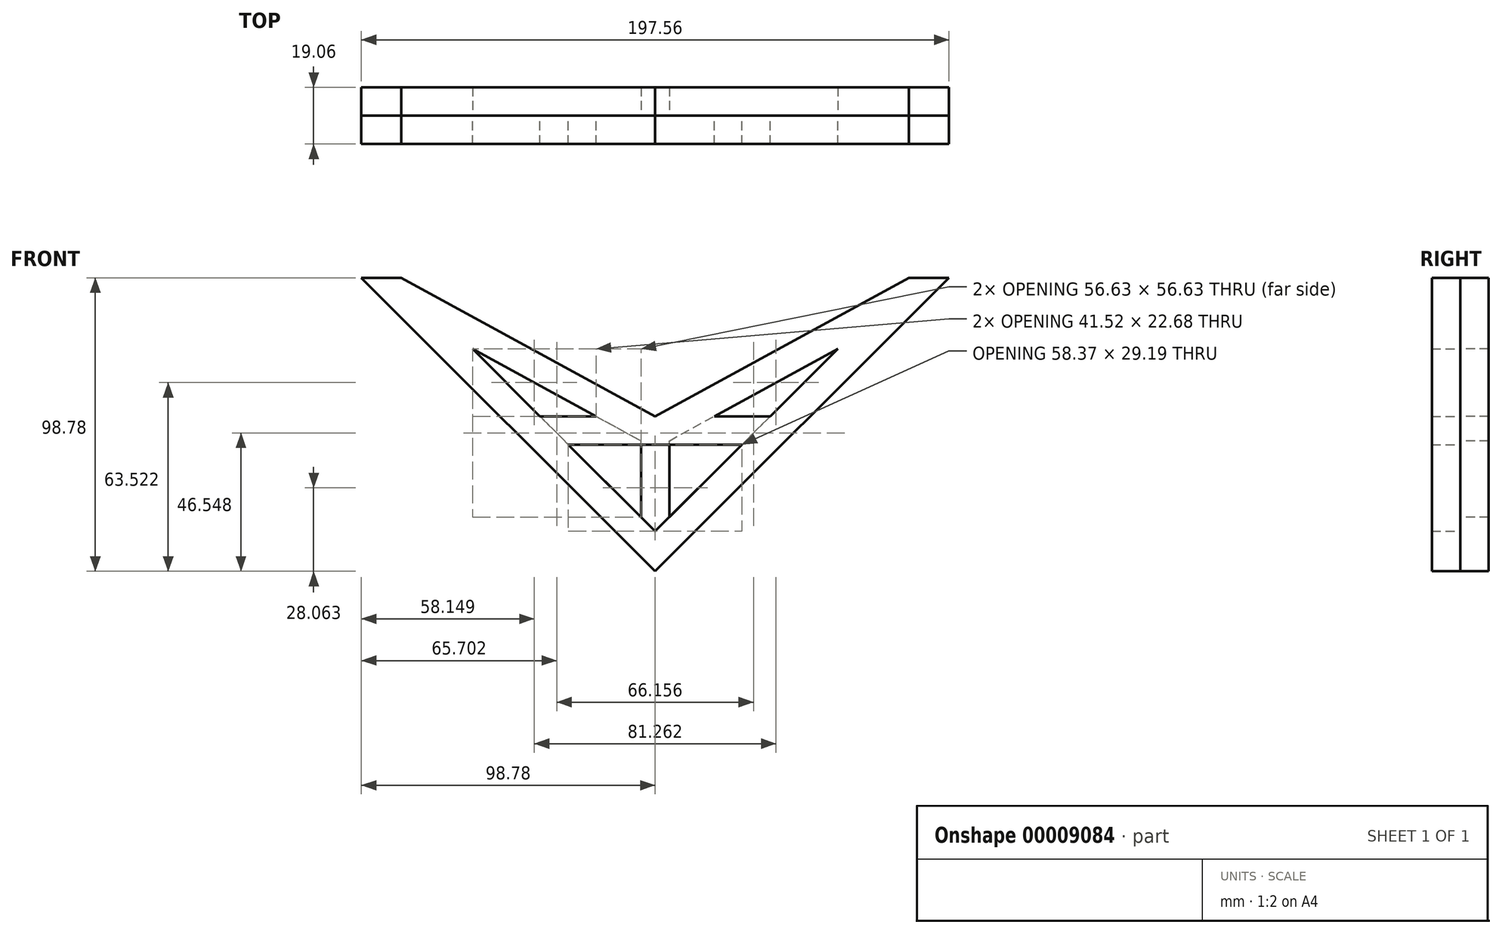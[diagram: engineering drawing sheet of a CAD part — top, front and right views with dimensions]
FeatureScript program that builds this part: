
annotation { "Feature Type Name" : "Feature", "Feature Type Description" : "" }
export const myFeature = defineFeature(function(context is Context, id is Id, definition is map)
    precondition{}
    {
        {
            var Q0;
            Q0=qCreatedBy(makeId("Front.planeOp"),FACE);
            var sketch = newSketch(context, id + "F0", { "sketchPlane" : qUnion([Q0])});
            skLineSegment(sketch, "E0", {"start": v(0, 0) * mm, "end": v(-98.78, 98.78) * mm});
            skLineSegment(sketch, "E1", {"start": v(0, 0) * mm, "end": v(98.78, 98.78) * mm});
            skLineSegment(sketch, "E2", {"start": v(0, 13.47) * mm, "end": v(-29.19, 42.66) * mm});
            skLineSegment(sketch, "E3", {"start": v(-29.19, 42.66) * mm, "end": v(29.19, 42.66) * mm});
            skLineSegment(sketch, "E4", {"start": v(29.19, 42.66) * mm, "end": v(0, 13.47) * mm});
            skLineSegment(sketch, "E5", {"start": v(38.71, 52.18) * mm, "end": v(-38.71, 52.18) * mm});
            skLineSegment(sketch, "E6", {"start": v(0, 52.18) * mm, "end": v(-85.31, 98.78) * mm});
            skLineSegment(sketch, "E7", {"start": v(-98.78, 98.78) * mm, "end": v(-85.31, 98.78) * mm});
            skLineSegment(sketch, "E8", {"start": v(98.78, 98.78) * mm, "end": v(85.31, 98.78) * mm});
            skLineSegment(sketch, "E9", {"start": v(85.31, 98.78) * mm, "end": v(0, 52.18) * mm});
            skLineSegment(sketch, "E10", {"start": v(38.71, 52.18) * mm, "end": v(61.4, 74.86) * mm});
            skLineSegment(sketch, "E11", {"start": v(61.4, 74.86) * mm, "end": v(19.87, 52.18) * mm});
            skLineSegment(sketch, "E12", {"start": v(-38.71, 52.18) * mm, "end": v(-61.4, 74.86) * mm});
            skLineSegment(sketch, "E13", {"start": v(-61.4, 74.86) * mm, "end": v(-19.87, 52.18) * mm});
            skLineSegment(sketch, "E14", {"start": v(-19.87, 52.18) * mm, "end": v(19.87, 52.18) * mm});
            skLineSegment(sketch, "E15", {"start": v(-38.71, 52.18) * mm, "end": v(-29.19, 42.66) * mm});
            skLineSegment(sketch, "E16", {"start": v(29.19, 42.66) * mm, "end": v(38.71, 52.18) * mm});
            skLineSegment(sketch, "E17", {"start": v(0, 0) * mm, "end": v(0, 13.47) * mm, "construction": true});
            skLineSegment(sketch, "E18", {"start": v(-4.76, 18.23) * mm, "end": v(-4.76, 42.66) * mm});
            skLineSegment(sketch, "E19", {"start": v(4.76, 18.23) * mm, "end": v(4.76, 42.66) * mm});
            skLineSegment(sketch, "E20", {"start": v(-19.87, 52.18) * mm, "end": v(0, 41.33) * mm});
            skLineSegment(sketch, "E21", {"start": v(0, 41.33) * mm, "end": v(19.87, 52.18) * mm});
            skLineSegment(sketch, "E22", {"start": v(-4.76, 42.66) * mm, "end": v(-4.76, 43.93) * mm});
            skLineSegment(sketch, "E23", {"start": v(4.76, 42.66) * mm, "end": v(4.76, 43.93) * mm});
            skSolve(sketch);
        }
        {
            var Q0;
            {var subQ4=sQuery(id+"F0.wireOp",EDGE,"E15");Q0=makeQuery(id+"F0.imprint","IMPRINT",FACE,{"disambiguationData":[TD([[makeQuery(id+"F0.imprint","IMPRINT",EDGE,{"derivedFrom":subQ4}),1.0]])]});}
            var Q1;
            {var subQ5=sQuery(id+"F0.wireOp",EDGE,"E3");var subQ7=sQuery(id+"F0.wireOp",EDGE,"E20");var subQ8=makeQuery(id+"F0.imprint","INTERSECT",VERTEX,{"derivedFrom":[subQ5,subQ7]});Q1=makeQuery(id+"F0.imprint","IMPRINT",FACE,{"disambiguationData":[TD([[makeQuery(id+"F0.imprint","IMPRINT",EDGE,{"disambiguationData":[TD([[subQ8,-1.0]])],"derivedFrom":subQ5}),1.0]])]});}
            var Q2;
            {var subQ4=sQuery(id+"F0.wireOp",EDGE,"E16");Q2=makeQuery(id+"F0.imprint","IMPRINT",FACE,{"disambiguationData":[TD([[makeQuery(id+"F0.imprint","IMPRINT",EDGE,{"derivedFrom":subQ4}),1.0]])]});}
            var Q3;
            Q3=makeQuery(id+"F0.imprint","IMPRINT",FACE,{"disambiguationData":[TD([[makeQuery(id+"F0.imprint","IMPRINT",EDGE,{"derivedFrom":sQuery(id+"F0.wireOp",EDGE,"E0")}),-1.0]])]});
            var Q4;
            {var subQ0=sQuery(id+"F0.wireOp",EDGE,"E23");Q4=makeQuery(id+"F0.imprint","IMPRINT",FACE,{"disambiguationData":[TD([[makeQuery(id+"F0.imprint","IMPRINT",EDGE,{"derivedFrom":subQ0}),1.0]])]});}
            var Q5;
            {var subQ0=sQuery(id+"F0.wireOp",EDGE,"E22");Q5=makeQuery(id+"F0.imprint","IMPRINT",FACE,{"disambiguationData":[TD([[makeQuery(id+"F0.imprint","IMPRINT",EDGE,{"derivedFrom":subQ0}),-1.0]])]});}
            extrude(context, id + "F1", {"entities" : qUnion([Q0, Q1, Q2, Q3, Q4, Q5]), "depth" : 9.52 * mm});
        }
        {
            var Q0;
            {var subQ5=sQuery(id+"F0.wireOp",EDGE,"E3");var subQ7=sQuery(id+"F0.wireOp",EDGE,"E20");var subQ8=makeQuery(id+"F0.imprint","INTERSECT",VERTEX,{"derivedFrom":[subQ5,subQ7]});Q0=makeQuery(id+"F0.imprint","IMPRINT",FACE,{"disambiguationData":[TD([[makeQuery(id+"F0.imprint","IMPRINT",EDGE,{"disambiguationData":[TD([[subQ8,-1.0]])],"derivedFrom":subQ5}),1.0]])]});}
            var Q1;
            {var subQ0=sQuery(id+"F0.wireOp",EDGE,"E22");Q1=makeQuery(id+"F0.imprint","IMPRINT",FACE,{"disambiguationData":[TD([[makeQuery(id+"F0.imprint","IMPRINT",EDGE,{"derivedFrom":subQ0}),-1.0]])]});}
            var Q2;
            {var subQ0=sQuery(id+"F0.wireOp",EDGE,"E23");Q2=makeQuery(id+"F0.imprint","IMPRINT",FACE,{"disambiguationData":[TD([[makeQuery(id+"F0.imprint","IMPRINT",EDGE,{"derivedFrom":subQ0}),1.0]])]});}
            var Q3;
            Q3=makeQuery(id+"F0.imprint","IMPRINT",FACE,{"disambiguationData":[TD([[makeQuery(id+"F0.imprint","IMPRINT",EDGE,{"derivedFrom":sQuery(id+"F0.wireOp",EDGE,"E0")}),-1.0]])]});
            var Q4;
            {var subQ1=sQuery(id+"F0.wireOp",EDGE,"E3");var subQ3=sQuery(id+"F0.wireOp",EDGE,"E20");var subQ5=makeQuery(id+"F0.imprint","INTERSECT",VERTEX,{"derivedFrom":[subQ1,subQ3]});Q4=makeQuery(id+"F0.imprint","IMPRINT",FACE,{"disambiguationData":[TD([[makeQuery(id+"F0.imprint","IMPRINT",EDGE,{"disambiguationData":[TD([[subQ5,-1.0]])],"derivedFrom":subQ1}),-1.0]])]});}
            var Q5;
            {var subQ7=sQuery(id+"F0.wireOp",EDGE,"E18");Q5=makeQuery(id+"F0.imprint","IMPRINT",FACE,{"disambiguationData":[TD([[makeQuery(id+"F0.imprint","IMPRINT",EDGE,{"derivedFrom":subQ7}),-1.0]])]});}
            extrude(context, id + "F2", {"entities" : qUnion([Q0, Q1, Q2, Q3, Q4, Q5]), "oppositeDirection" : true, "depth" : 9.52 * mm});
        }
    });
